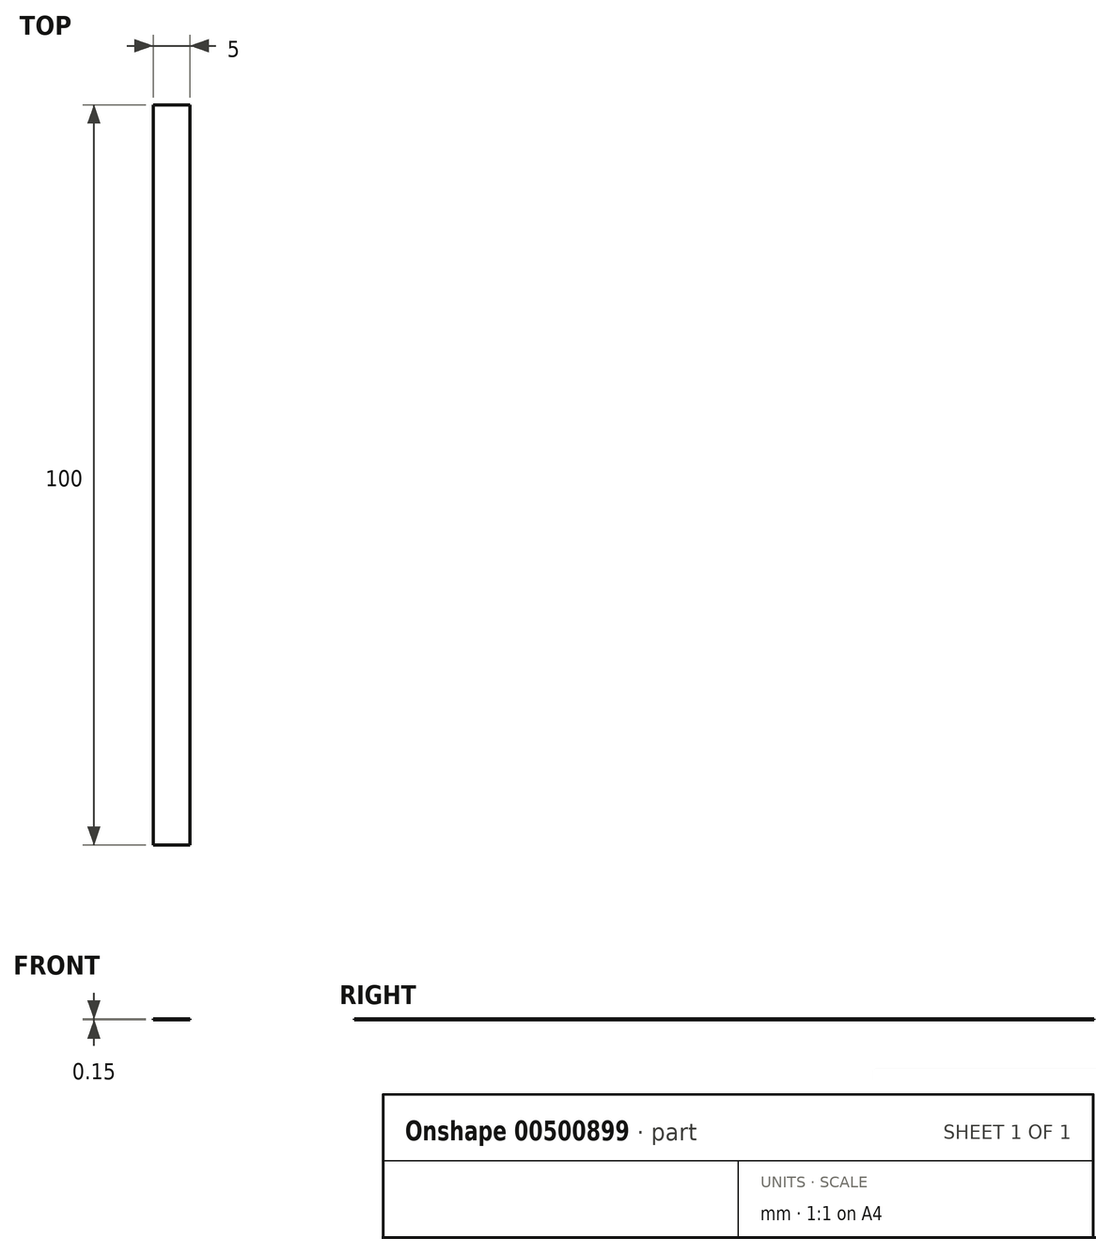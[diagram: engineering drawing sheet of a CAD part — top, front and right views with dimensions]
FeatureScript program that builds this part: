
annotation { "Feature Type Name" : "Feature", "Feature Type Description" : "" }
export const myFeature = defineFeature(function(context is Context, id is Id, definition is map)
    precondition{}
    {
        {
            var Q0;
            Q0=qCreatedBy(makeId("Top.planeOp"),FACE);
            var sketch = newSketch(context, id + "F0", { "sketchPlane" : qUnion([Q0])});
            skLineSegment(sketch, "E0.bottom", {"start": v(-2.5, -50) * mm, "end": v(2.5, -50) * mm});
            skLineSegment(sketch, "E0.top", {"start": v(-2.5, 50) * mm, "end": v(2.5, 50) * mm});
            skLineSegment(sketch, "E0.left", {"start": v(-2.5, -50) * mm, "end": v(-2.5, 50) * mm});
            skLineSegment(sketch, "E0.right", {"start": v(2.5, -50) * mm, "end": v(2.5, 50) * mm});
            skPoint(sketch, "E0.middle", {"position": v(0, 0) * mm});
            skSolve(sketch);
        }
        {
            var Q0;
            Q0=makeQuery(id+"F0.imprint","IMPRINT",FACE,{"disambiguationData":[TD([[makeQuery(id+"F0.imprint","IMPRINT",EDGE,{"derivedFrom":sQuery(id+"F0.wireOp",EDGE,"E0.bottom")}),1.0]])]});
            extrude(context, id + "F1", {"entities" : qUnion([Q0]), "depth" : .15 * mm, "offsetDistance" : 25 * mm});
        }
    });
